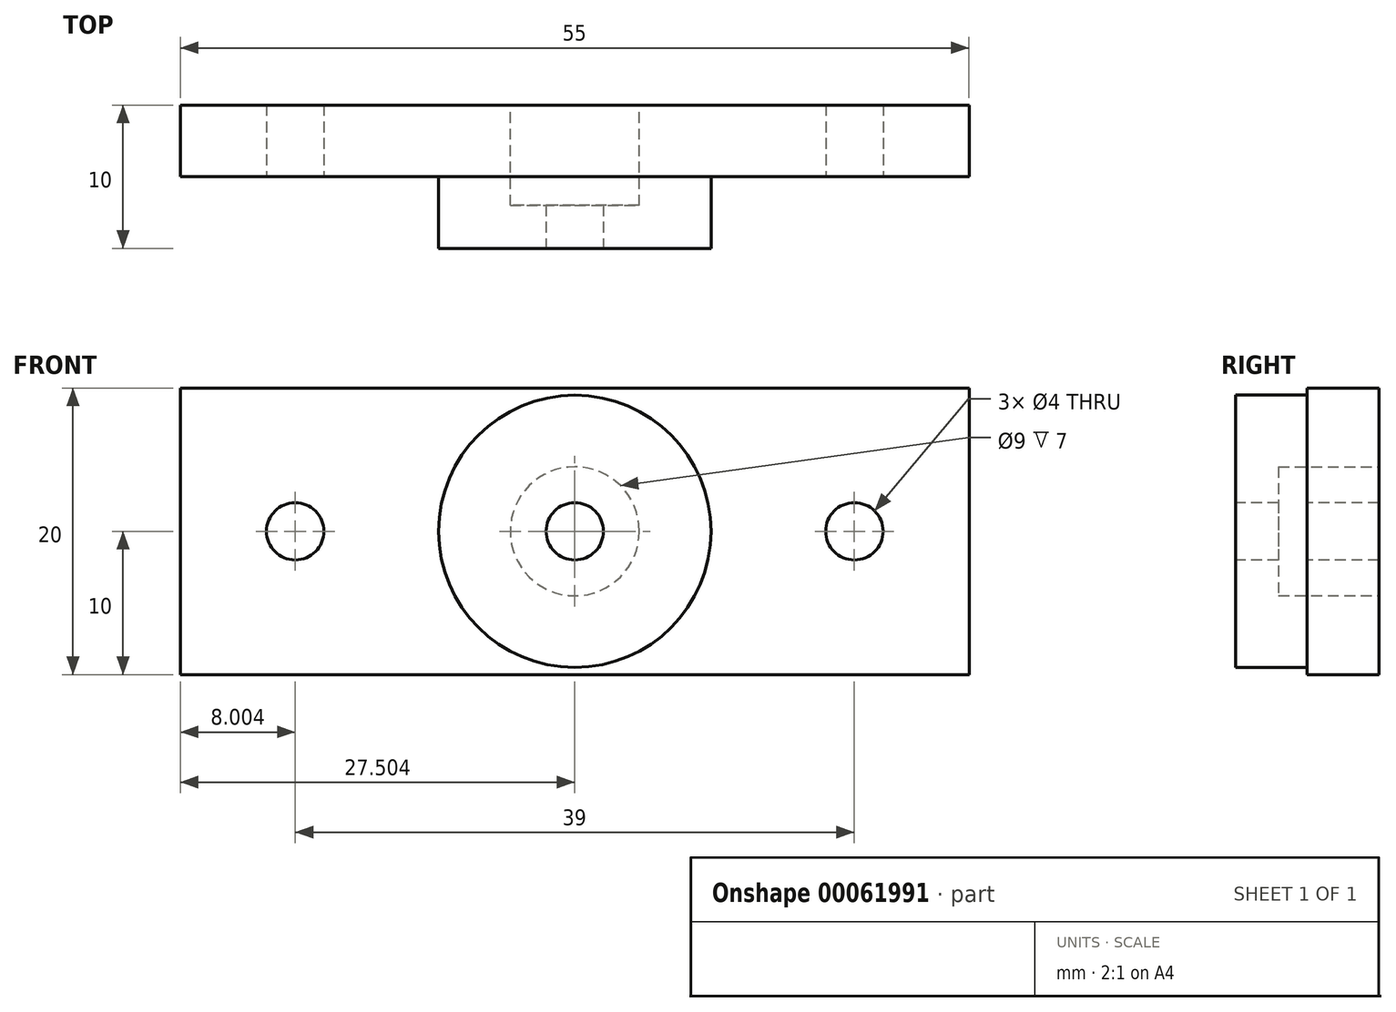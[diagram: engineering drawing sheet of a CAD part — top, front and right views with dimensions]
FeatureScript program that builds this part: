
annotation { "Feature Type Name" : "Feature", "Feature Type Description" : "" }
export const myFeature = defineFeature(function(context is Context, id is Id, definition is map)
    precondition{}
    {
        {
            var Q0;
            Q0=qCreatedBy(makeId("Top.planeOp"),FACE);
            var sketch = newSketch(context, id + "F0", { "sketchPlane" : qUnion([Q0])});
            skLineSegment(sketch, "E0.bottom", {"start": v(-12.37, 0) * mm, "end": v(42.63, 0) * mm});
            skLineSegment(sketch, "E0.right", {"start": v(42.63, 0) * mm, "end": v(42.63, 5) * mm});
            skLineSegment(sketch, "E1", {"start": v(-12.37, 5) * mm, "end": v(42.63, 5) * mm});
            skLineSegment(sketch, "E2", {"start": v(-12.37, 0) * mm, "end": v(-12.37, 5) * mm});
            skSolve(sketch);
        }
        {
            var Q0;
            Q0=makeQuery(id+"F0.imprint","IMPRINT",FACE,{"disambiguationData":[TD([[makeQuery(id+"F0.imprint","IMPRINT",EDGE,{"derivedFrom":sQuery(id+"F0.wireOp",EDGE,"E0.bottom")}),1.0]])]});
            extrude(context, id + "F1", {"entities" : qUnion([Q0]), "depth" : 20 * mm});
        }
        {
            var Q0;
            Q0=makeQuery(id+"F1.opExtrude","SWEPT_FACE",FACE,{"disambiguationData":[OSD([sQuery(id+"F0.wireOp",EDGE,"E0.bottom")])]});
            var sketch = newSketch(context, id + "F2", { "sketchPlane" : qUnion([Q0])});
            skCircle(sketch, "E3", {"center": v(15.13, 10) * mm, "radius": 9.5 * mm});
            skPoint(sketch, "E3.centerSnap0", {"position": v(15.13, 20) * mm});
            skPoint(sketch, "E3.centerSnap1", {"position": v(42.63, 10) * mm});
            skSolve(sketch);
        }
        {
            var Q0;
            Q0=makeQuery(id+"F2.imprint","IMPRINT",FACE,{"disambiguationData":[TD([[makeQuery(id+"F2.imprint","IMPRINT",EDGE,{"derivedFrom":sQuery(id+"F2.wireOp",EDGE,"E3")}),1.0]])]});
            extrude(context, id + "F3", {"entities" : qUnion([Q0]), "operationType" : NewBodyOperationType.ADD, "depth" : 5 * mm});
        }
        {
            var Q0;
            Q0=makeQuery(id+"F3.opExtrude","CAP_FACE",FACE,{"disambiguationData":[OSD([sQuery(id+"F2.wireOp",EDGE,"E3")])],"isStart":false});
            var sketch = newSketch(context, id + "F4", { "sketchPlane" : qUnion([Q0])});
            skCircle(sketch, "E4", {"center": v(15.13, 10) * mm, "radius": 2 * mm});
            skSolve(sketch);
        }
        {
            var Q0;
            Q0=makeQuery(id+"F4.imprint","IMPRINT",FACE,{"disambiguationData":[TD([[makeQuery(id+"F4.imprint","IMPRINT",EDGE,{"derivedFrom":sQuery(id+"F4.wireOp",EDGE,"E4")}),1.0]])]});
            extrude(context, id + "F5", {"entities" : qUnion([Q0]), "operationType" : NewBodyOperationType.REMOVE, "endBound" : BoundingType.THROUGH_ALL, "oppositeDirection" : true, "depth" : 25 * mm});
        }
        {
            var Q0;
            Q0=makeQuery(id+"F1.opExtrude","SWEPT_FACE",FACE,{"disambiguationData":[OSD([sQuery(id+"F0.wireOp",EDGE,"E1")])]});
            var sketch = newSketch(context, id + "F6", { "sketchPlane" : qUnion([Q0])});
            skCircle(sketch, "E5", {"center": v(-15.13, 10) * mm, "radius": 4.5 * mm});
            skSolve(sketch);
        }
        {
            var Q0;
            Q0=makeQuery(id+"F6.imprint","IMPRINT",FACE,{"disambiguationData":[TD([[makeQuery(id+"F6.imprint","IMPRINT",EDGE,{"derivedFrom":sQuery(id+"F6.wireOp",EDGE,"E5")}),1.0]])]});
            extrude(context, id + "F7", {"entities" : qUnion([Q0]), "operationType" : NewBodyOperationType.REMOVE, "oppositeDirection" : true, "depth" : 7 * mm});
        }
        {
            var Q0;
            Q0=makeQuery(id+"F1.opExtrude","SWEPT_FACE",FACE,{"disambiguationData":[OSD([sQuery(id+"F0.wireOp",EDGE,"E0.bottom")])]});
            var sketch = newSketch(context, id + "F8", { "sketchPlane" : qUnion([Q0])});
            skCircle(sketch, "E6", {"center": v(-4.37, 10) * mm, "radius": 2 * mm});
            skPoint(sketch, "E6.centerSnap0", {"position": v(-12.37, 10) * mm});
            skCircle(sketch, "E7", {"center": v(34.63, 10) * mm, "radius": 2 * mm});
            skPoint(sketch, "E7.centerSnap0", {"position": v(42.63, 10) * mm});
            skSolve(sketch);
        }
        {
            var Q0;
            Q0=makeQuery(id+"F8.imprint","IMPRINT",FACE,{"disambiguationData":[TD([[makeQuery(id+"F8.imprint","IMPRINT",EDGE,{"derivedFrom":sQuery(id+"F8.wireOp",EDGE,"E6")}),1.0]])]});
            var Q1;
            Q1=makeQuery(id+"F8.imprint","IMPRINT",FACE,{"disambiguationData":[TD([[makeQuery(id+"F8.imprint","IMPRINT",EDGE,{"derivedFrom":sQuery(id+"F8.wireOp",EDGE,"E7")}),1.0]])]});
            extrude(context, id + "F9", {"entities" : qUnion([Q0, Q1]), "operationType" : NewBodyOperationType.REMOVE, "oppositeDirection" : true, "depth" : 25 * mm});
        }
    });
